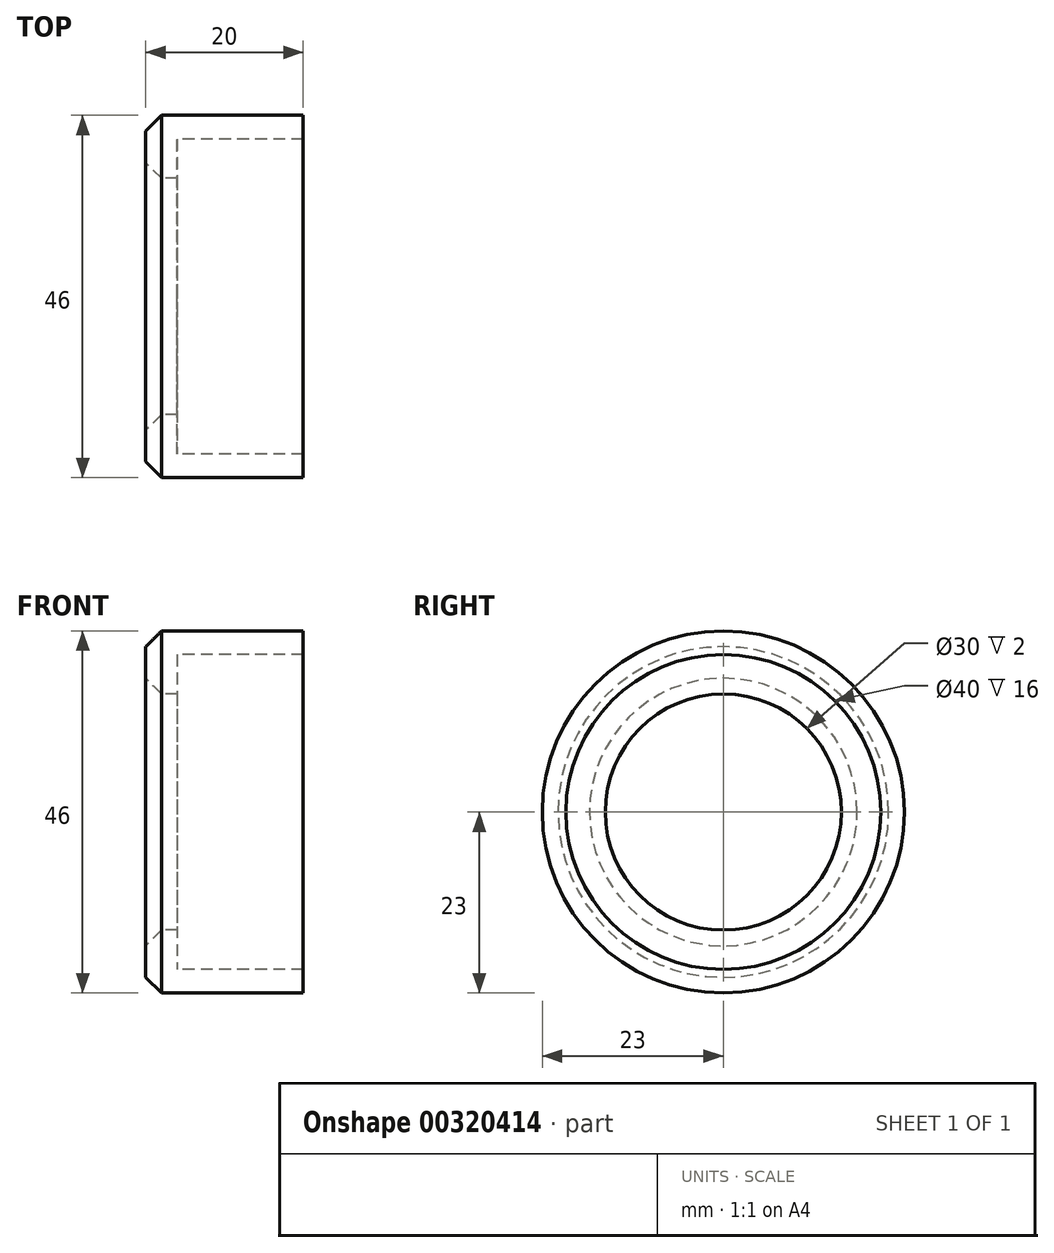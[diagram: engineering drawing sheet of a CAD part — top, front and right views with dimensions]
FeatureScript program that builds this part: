
annotation { "Feature Type Name" : "Feature", "Feature Type Description" : "" }
export const myFeature = defineFeature(function(context is Context, id is Id, definition is map)
    precondition{}
    {
        {
            var Q0;
            Q0=qCreatedBy(makeId("Front.planeOp"),FACE);
            var sketch = newSketch(context, id + "F0", { "sketchPlane" : qUnion([Q0])});
            skLineSegment(sketch, "E0", {"start": v(8.35, 15) * mm, "end": v(8.35, 20) * mm});
            skLineSegment(sketch, "E1", {"start": v(8.35, 20) * mm, "end": v(8.35, 23) * mm});
            skLineSegment(sketch, "E2", {"start": v(8.35, 23) * mm, "end": v(28.35, 23) * mm});
            skLineSegment(sketch, "E3", {"start": v(28.35, 23) * mm, "end": v(28.35, 20) * mm});
            skLineSegment(sketch, "E4", {"start": v(12.35, 20) * mm, "end": v(28.35, 20) * mm});
            skLineSegment(sketch, "E5", {"start": v(8.35, 15) * mm, "end": v(12.35, 15) * mm});
            skLineSegment(sketch, "E6", {"start": v(12.35, 20) * mm, "end": v(12.35, 15) * mm});
            skSolve(sketch);
        }
        {
            var Q0;
            Q0=qCreatedBy(makeId("Front.planeOp"),FACE);
            var sketch = newSketch(context, id + "F1", { "sketchPlane" : qUnion([Q0])});
            skLineSegment(sketch, "E7", {"start": v(-53.95, 0) * mm, "end": v(56.7, 0) * mm});
            skSolve(sketch);
        }
        {
            var Q0;
            Q0=makeQuery(id+"F0.imprint","IMPRINT",FACE,{"disambiguationData":[TD([[makeQuery(id+"F0.imprint","IMPRINT",EDGE,{"derivedFrom":sQuery(id+"F0.wireOp",EDGE,"E0")}),-1.0]])]});
            var Q1;
            Q1=sQuery(id+"F1.wireOp",EDGE,"E7");
            revolve(context, id + "F2", {"entities" : qUnion([Q0]), "axis" : qUnion([Q1]), "revolveType" : RevolveType.FULL});
        }
        {
            var Q0;
            Q0=makeQuery(id+"F2.opRevolve","SWEPT_EDGE",EDGE,{"disambiguationData":[OSD([sQuery(id+"F0.wireOp",EDGE,"E1"),sQuery(id+"F0.wireOp",EDGE,"E2")])]});
            chamfer(context, id + "F3", {"entities" : qUnion([Q0]), "width" : 2 * mm, "tangentPropagation" : true});
        }
        {
            var Q0;
            Q0=makeQuery(id+"F2.opRevolve","SWEPT_EDGE",EDGE,{"disambiguationData":[OSD([sQuery(id+"F0.wireOp",EDGE,"E0"),sQuery(id+"F0.wireOp",EDGE,"E5")])]});
            chamfer(context, id + "F4", {"entities" : qUnion([Q0]), "width" : 2 * mm, "tangentPropagation" : true});
        }
    });
